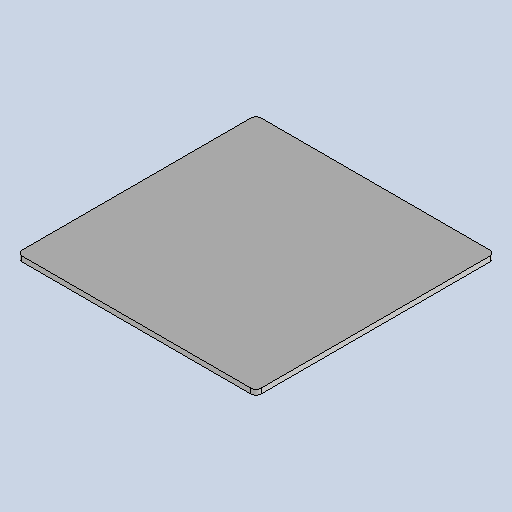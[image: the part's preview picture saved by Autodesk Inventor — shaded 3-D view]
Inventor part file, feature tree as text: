
AUTODESK INVENTOR PART (.ipt)
format: ipt  version: 2025.1 (Build 291241020, 241B)  size: 184,832 bytes
history: native  units: mm
features: other x2, sheet_metal_op x1, chamfer x1, sketch x1
ambient origin geometry x8: Origin, YZ Plane, XZ Plane, XY Plane, X Axis, Y Axis, Z Axis, Center Point
bodies: Body1 (feature_tree)
feature tree (5):
  sheet_metal_op  "Face3"
  chamfer  "Corner Round1"
  sketch  "Sketch1"  dims[d154=94.0mm d155=94.0mm d156=2.0mm d178=2.0mm]
  other  "Plate5"
  other  "Definition1"
